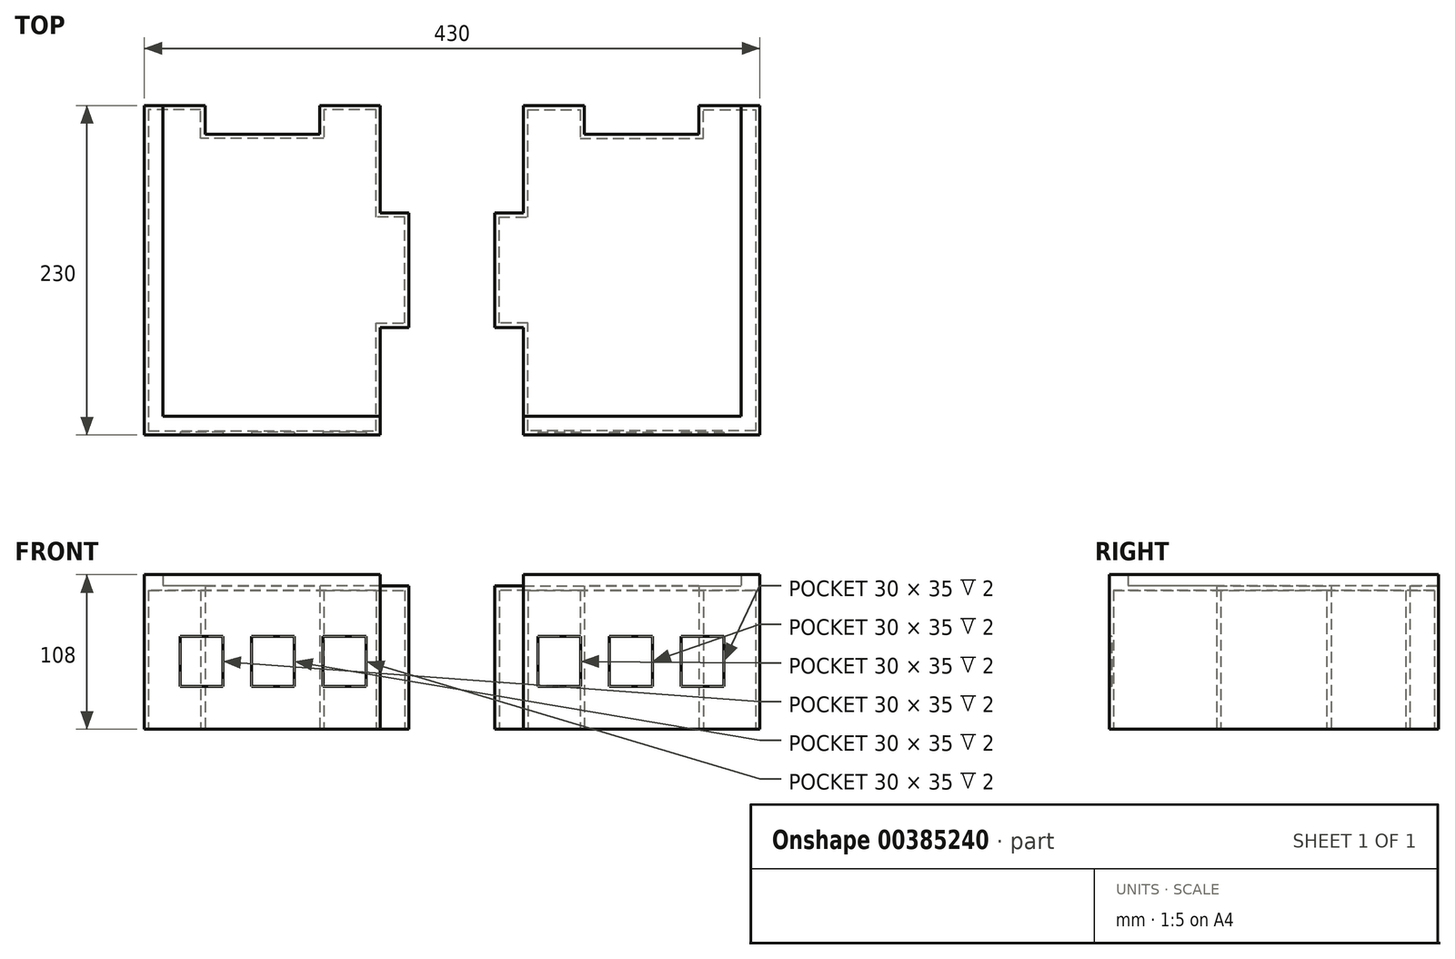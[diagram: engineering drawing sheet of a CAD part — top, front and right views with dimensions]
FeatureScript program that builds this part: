
annotation { "Feature Type Name" : "Feature", "Feature Type Description" : "" }
export const myFeature = defineFeature(function(context is Context, id is Id, definition is map)
    precondition{}
    {
        {
            var Q0;
            Q0=qCreatedBy(makeId("Top.planeOp"),FACE);
            var sketch = newSketch(context, id + "F0", { "sketchPlane" : qUnion([Q0])});
            skLineSegment(sketch, "E0.bottom", {"start": v(0, 0) * mm, "end": v(42.5, 0) * mm});
            skLineSegment(sketch, "E0.top", {"start": v(0, -230) * mm, "end": v(165, -230) * mm});
            skLineSegment(sketch, "E0.left", {"start": v(0, 0) * mm, "end": v(0, -75) * mm});
            skLineSegment(sketch, "E0.right", {"start": v(165, 0) * mm, "end": v(165, -230) * mm});
            skLineSegment(sketch, "E1.bottom", {"start": v(-20, -155) * mm, "end": v(0, -155) * mm});
            skLineSegment(sketch, "E1.top", {"start": v(-20, -75) * mm, "end": v(0, -75) * mm});
            skLineSegment(sketch, "E1.left", {"start": v(-20, -155) * mm, "end": v(-20, -75) * mm});
            skPoint(sketch, "E1.middle", {"position": v(0, -115) * mm});
            skPoint(sketch, "E1.right.start.orphan", {"position": v(20, -155) * mm});
            skPoint(sketch, "E2.orphan", {"position": v(20, -75) * mm});
            skLineSegment(sketch, "E3.trimOffspring", {"start": v(0, -155) * mm, "end": v(0, -230) * mm});
            skLineSegment(sketch, "E4.bottom", {"start": v(122.5, -20) * mm, "end": v(42.5, -20) * mm});
            skLineSegment(sketch, "E4.left", {"start": v(122.5, -20) * mm, "end": v(122.5, 0) * mm});
            skLineSegment(sketch, "E4.right", {"start": v(42.5, -20) * mm, "end": v(42.5, 0) * mm});
            skPoint(sketch, "E4.middle", {"position": v(82.5, 0) * mm});
            skPoint(sketch, "E4.top.end.orphan", {"position": v(42.5, 20) * mm});
            skPoint(sketch, "E5.orphan", {"position": v(122.5, 20) * mm});
            skLineSegment(sketch, "E6.trimOffspring", {"start": v(122.5, 0) * mm, "end": v(165, 0) * mm});
            skLineSegment(sketch, "E7", {"start": v(0, -75) * mm, "end": v(0, 0) * mm});
            skLineSegment(sketch, "E8", {"start": v(42.5, -20) * mm, "end": v(122.5, -20) * mm});
            skLineSegment(sketch, "E9.0", {"start": v(2.5, -152.5) * mm, "end": v(2.5, -227.5) * mm});
            skLineSegment(sketch, "E9.1", {"start": v(125, -22.5) * mm, "end": v(40, -22.5) * mm});
            skLineSegment(sketch, "E9.2", {"start": v(125, -22.5) * mm, "end": v(125, -2.5) * mm});
            skLineSegment(sketch, "E9.3", {"start": v(125, -2.5) * mm, "end": v(162.5, -2.5) * mm});
            skLineSegment(sketch, "E9.4", {"start": v(162.5, -2.5) * mm, "end": v(162.5, -227.5) * mm});
            skLineSegment(sketch, "E9.5", {"start": v(40, -22.5) * mm, "end": v(40, -2.5) * mm});
            skLineSegment(sketch, "E9.6", {"start": v(2.5, -227.5) * mm, "end": v(162.5, -227.5) * mm});
            skLineSegment(sketch, "E9.7", {"start": v(2.5, -2.5) * mm, "end": v(40, -2.5) * mm});
            skLineSegment(sketch, "E9.8", {"start": v(2.5, -77.5) * mm, "end": v(2.5, -2.5) * mm});
            skLineSegment(sketch, "E9.9", {"start": v(-17.5, -77.5) * mm, "end": v(2.5, -77.5) * mm});
            skLineSegment(sketch, "E9.10", {"start": v(-17.5, -152.5) * mm, "end": v(-17.5, -77.5) * mm});
            skLineSegment(sketch, "E9.11", {"start": v(-17.5, -152.5) * mm, "end": v(2.5, -152.5) * mm});
            skSolve(sketch);
        }
        {
            var Q0;
            Q0=makeQuery(id+"F0.imprint","IMPRINT",FACE,{"disambiguationData":[TD([[makeQuery(id+"F0.imprint","IMPRINT",EDGE,{"derivedFrom":sQuery(id+"F0.wireOp",EDGE,"E0.bottom")}),-1.0]])]});
            extrude(context, id + "F1", {"entities" : qUnion([Q0]), "depth" : 100 * mm});
        }
        {
            var Q0;
            Q0=makeQuery(id+"F1.opExtrude","CAP_FACE",FACE,{"disambiguationData":[OSD([sQuery(id+"F0.wireOp",EDGE,"E0.bottom"),sQuery(id+"F0.wireOp",EDGE,"E0.top"),sQuery(id+"F0.wireOp",EDGE,"E0.right"),sQuery(id+"F0.wireOp",EDGE,"E1.bottom"),sQuery(id+"F0.wireOp",EDGE,"E1.top"),sQuery(id+"F0.wireOp",EDGE,"E1.left"),sQuery(id+"F0.wireOp",EDGE,"E3.trimOffspring"),sQuery(id+"F0.wireOp",EDGE,"E4.left"),sQuery(id+"F0.wireOp",EDGE,"E4.right"),sQuery(id+"F0.wireOp",EDGE,"E6.trimOffspring"),sQuery(id+"F0.wireOp",EDGE,"E7"),sQuery(id+"F0.wireOp",EDGE,"E8"),sQuery(id+"F0.wireOp",EDGE,"E9.0"),sQuery(id+"F0.wireOp",EDGE,"E9.1"),sQuery(id+"F0.wireOp",EDGE,"E9.2"),sQuery(id+"F0.wireOp",EDGE,"E9.3"),sQuery(id+"F0.wireOp",EDGE,"E9.4"),sQuery(id+"F0.wireOp",EDGE,"E9.5"),sQuery(id+"F0.wireOp",EDGE,"E9.6"),sQuery(id+"F0.wireOp",EDGE,"E9.7"),sQuery(id+"F0.wireOp",EDGE,"E9.8"),sQuery(id+"F0.wireOp",EDGE,"E9.9"),sQuery(id+"F0.wireOp",EDGE,"E9.10"),sQuery(id+"F0.wireOp",EDGE,"E9.11")])],"isStart":false});
            var sketch = newSketch(context, id + "F2", { "sketchPlane" : qUnion([Q0])});
            skLineSegment(sketch, "E10", {"start": v(0, -230) * mm, "end": v(165, -230) * mm});
            skLineSegment(sketch, "E11", {"start": v(165, -230) * mm, "end": v(165, 0) * mm});
            skLineSegment(sketch, "E12", {"start": v(165, 0) * mm, "end": v(122.5, 0) * mm});
            skLineSegment(sketch, "E13", {"start": v(122.5, 0) * mm, "end": v(122.5, -20) * mm});
            skLineSegment(sketch, "E14", {"start": v(122.5, -20) * mm, "end": v(42.5, -20) * mm});
            skLineSegment(sketch, "E15", {"start": v(42.5, -20) * mm, "end": v(42.5, 0) * mm});
            skLineSegment(sketch, "E16", {"start": v(42.5, 0) * mm, "end": v(0, 0) * mm});
            skLineSegment(sketch, "E17", {"start": v(0, 0) * mm, "end": v(0, -75) * mm});
            skLineSegment(sketch, "E18", {"start": v(0, -75) * mm, "end": v(-20, -75) * mm});
            skLineSegment(sketch, "E19", {"start": v(-20, -75) * mm, "end": v(-20, -155) * mm});
            skLineSegment(sketch, "E20", {"start": v(-20, -155) * mm, "end": v(0, -155) * mm});
            skLineSegment(sketch, "E21", {"start": v(0, -155) * mm, "end": v(0, -230) * mm});
            skSolve(sketch);
        }
        {
            var Q0;
            Q0=qSketchRegion(id+"F2",true);
            extrude(context, id + "F3", {"entities" : qUnion([Q0]), "operationType" : NewBodyOperationType.ADD, "oppositeDirection" : true, "depth" : 3 * mm});
        }
        {
            var Q0;
            Q0=makeQuery(id+"F3.boolean.opBoolean","MERGE",FACE,{"derivedFrom":[makeQuery(id+"F1.opExtrude","CAP_FACE",FACE,{"disambiguationData":[OSD([sQuery(id+"F0.wireOp",EDGE,"E0.bottom"),sQuery(id+"F0.wireOp",EDGE,"E0.top"),sQuery(id+"F0.wireOp",EDGE,"E0.right"),sQuery(id+"F0.wireOp",EDGE,"E1.bottom"),sQuery(id+"F0.wireOp",EDGE,"E1.top"),sQuery(id+"F0.wireOp",EDGE,"E1.left"),sQuery(id+"F0.wireOp",EDGE,"E3.trimOffspring"),sQuery(id+"F0.wireOp",EDGE,"E4.left"),sQuery(id+"F0.wireOp",EDGE,"E4.right"),sQuery(id+"F0.wireOp",EDGE,"E6.trimOffspring"),sQuery(id+"F0.wireOp",EDGE,"E7"),sQuery(id+"F0.wireOp",EDGE,"E8"),sQuery(id+"F0.wireOp",EDGE,"E9.0"),sQuery(id+"F0.wireOp",EDGE,"E9.1"),sQuery(id+"F0.wireOp",EDGE,"E9.2"),sQuery(id+"F0.wireOp",EDGE,"E9.3"),sQuery(id+"F0.wireOp",EDGE,"E9.4"),sQuery(id+"F0.wireOp",EDGE,"E9.5"),sQuery(id+"F0.wireOp",EDGE,"E9.6"),sQuery(id+"F0.wireOp",EDGE,"E9.7"),sQuery(id+"F0.wireOp",EDGE,"E9.8"),sQuery(id+"F0.wireOp",EDGE,"E9.9"),sQuery(id+"F0.wireOp",EDGE,"E9.10"),sQuery(id+"F0.wireOp",EDGE,"E9.11")])],"isStart":false}),makeQuery(id+"F3.opExtrude","CAP_FACE",FACE,{"disambiguationData":[OSD([sQuery(id+"F2.wireOp",EDGE,"E10"),sQuery(id+"F2.wireOp",EDGE,"E11"),sQuery(id+"F2.wireOp",EDGE,"E12"),sQuery(id+"F2.wireOp",EDGE,"E13"),sQuery(id+"F2.wireOp",EDGE,"E14"),sQuery(id+"F2.wireOp",EDGE,"E15"),sQuery(id+"F2.wireOp",EDGE,"E16"),sQuery(id+"F2.wireOp",EDGE,"E17"),sQuery(id+"F2.wireOp",EDGE,"E18"),sQuery(id+"F2.wireOp",EDGE,"E19"),sQuery(id+"F2.wireOp",EDGE,"E20"),sQuery(id+"F2.wireOp",EDGE,"E21")])],"isStart":true})]});
            var sketch = newSketch(context, id + "F4", { "sketchPlane" : qUnion([Q0])});
            skLineSegment(sketch, "E22.bottom", {"start": v(0, -230) * mm, "end": v(165, -230) * mm});
            skLineSegment(sketch, "E22.top", {"start": v(0, -217) * mm, "end": v(152, -217) * mm});
            skLineSegment(sketch, "E22.left", {"start": v(0, -230) * mm, "end": v(0, -217) * mm});
            skLineSegment(sketch, "E22.right", {"start": v(165, -230) * mm, "end": v(165, -217) * mm});
            skLineSegment(sketch, "E23.bottom", {"start": v(165, 0) * mm, "end": v(152, 0) * mm});
            skLineSegment(sketch, "E23.left", {"start": v(165, 0) * mm, "end": v(165, -217) * mm});
            skLineSegment(sketch, "E23.right", {"start": v(152, 0) * mm, "end": v(152, -217) * mm});
            skSolve(sketch);
        }
        {
            var Q0;
            Q0=makeQuery(id+"F4.imprint","IMPRINT",FACE,{"disambiguationData":[TD([[makeQuery(id+"F4.imprint","IMPRINT",EDGE,{"derivedFrom":sQuery(id+"F4.wireOp",EDGE,"E22.bottom")}),1.0]])]});
            extrude(context, id + "F5", {"entities" : qUnion([Q0]), "operationType" : NewBodyOperationType.ADD, "depth" : 8 * mm});
        }
        {
            var Q0;
            Q0=makeQuery(id+"F5.boolean.opBoolean","MERGE",FACE,{"derivedFrom":[makeQuery(id+"F1.opExtrude","SWEPT_FACE",FACE,{"disambiguationData":[OSD([sQuery(id+"F0.wireOp",EDGE,"E0.right")])]}),makeQuery(id+"F5.opExtrude","SWEPT_FACE",FACE,{"disambiguationData":[OSD([sQuery(id+"F4.wireOp",EDGE,"E22.right"),sQuery(id+"F4.wireOp",EDGE,"E23.left")])]})]});
            var sketch = newSketch(context, id + "F6", { "sketchPlane" : qUnion([Q0])});
            skLineSegment(sketch, "E24.bottom", {"start": v(0, 0) * mm, "end": v(-10, 0) * mm, "construction": true});
            skLineSegment(sketch, "E24.top", {"start": v(0, 30) * mm, "end": v(-10, 30) * mm, "construction": true});
            skLineSegment(sketch, "E24.left", {"start": v(0, 0) * mm, "end": v(0, 30) * mm, "construction": true});
            skLineSegment(sketch, "E24.right", {"start": v(-10, 0) * mm, "end": v(-10, 30) * mm, "construction": true});
            skLineSegment(sketch, "E25.bottom", {"start": v(-10, 30) * mm, "end": v(-40, 30) * mm});
            skLineSegment(sketch, "E25.top", {"start": v(-10, 65) * mm, "end": v(-40, 65) * mm});
            skLineSegment(sketch, "E25.left", {"start": v(-10, 30) * mm, "end": v(-10, 65) * mm});
            skLineSegment(sketch, "E25.right", {"start": v(-40, 30) * mm, "end": v(-40, 65) * mm});
            skLineSegment(sketch, "E26.bottom", {"start": v(-40, 30) * mm, "end": v(-60, 30) * mm, "construction": true});
            skLineSegment(sketch, "E26.top", {"start": v(-40, 65) * mm, "end": v(-60, 65) * mm, "construction": true});
            skLineSegment(sketch, "E26.left", {"start": v(-40, 30) * mm, "end": v(-40, 65) * mm, "construction": true});
            skLineSegment(sketch, "E26.right", {"start": v(-60, 30) * mm, "end": v(-60, 65) * mm, "construction": true});
            skLineSegment(sketch, "E27.bottom", {"start": v(-60, 30) * mm, "end": v(-90, 30) * mm});
            skLineSegment(sketch, "E27.top", {"start": v(-60, 65) * mm, "end": v(-90, 65) * mm});
            skLineSegment(sketch, "E27.left", {"start": v(-60, 30) * mm, "end": v(-60, 65) * mm});
            skLineSegment(sketch, "E27.right", {"start": v(-90, 30) * mm, "end": v(-90, 65) * mm});
            skLineSegment(sketch, "E28.bottom", {"start": v(-90, 30) * mm, "end": v(-110, 30) * mm, "construction": true});
            skLineSegment(sketch, "E28.top", {"start": v(-90, 65) * mm, "end": v(-110, 65) * mm, "construction": true});
            skLineSegment(sketch, "E28.left", {"start": v(-90, 30) * mm, "end": v(-90, 65) * mm, "construction": true});
            skLineSegment(sketch, "E28.right", {"start": v(-110, 30) * mm, "end": v(-110, 65) * mm, "construction": true});
            skLineSegment(sketch, "E29.bottom", {"start": v(-110, 30) * mm, "end": v(-140, 30) * mm});
            skLineSegment(sketch, "E29.top", {"start": v(-110, 65) * mm, "end": v(-140, 65) * mm});
            skLineSegment(sketch, "E29.left", {"start": v(-110, 30) * mm, "end": v(-110, 65) * mm});
            skLineSegment(sketch, "E29.right", {"start": v(-140, 30) * mm, "end": v(-140, 65) * mm});
            skLineSegment(sketch, "E30.bottom", {"start": v(-140, 30) * mm, "end": v(-160, 30) * mm, "construction": true});
            skLineSegment(sketch, "E30.top", {"start": v(-140, 65) * mm, "end": v(-160, 65) * mm, "construction": true});
            skLineSegment(sketch, "E30.left", {"start": v(-140, 30) * mm, "end": v(-140, 65) * mm, "construction": true});
            skLineSegment(sketch, "E30.right", {"start": v(-160, 30) * mm, "end": v(-160, 65) * mm, "construction": true});
            skLineSegment(sketch, "E31.bottom", {"start": v(-160, 30) * mm, "end": v(-190, 30) * mm});
            skLineSegment(sketch, "E31.top", {"start": v(-160, 65) * mm, "end": v(-190, 65) * mm});
            skLineSegment(sketch, "E31.left", {"start": v(-160, 30) * mm, "end": v(-160, 65) * mm});
            skLineSegment(sketch, "E31.right", {"start": v(-190, 30) * mm, "end": v(-190, 65) * mm});
            skSolve(sketch);
        }
        {
            var Q0;
            Q0=qSketchRegion(id+"F6",true);
            extrude(context, id + "F7", {"entities" : qUnion([Q0]), "operationType" : NewBodyOperationType.REMOVE, "oppositeDirection" : true, "depth" : 1 * mm});
        }
        {
            var Q0;
            Q0=makeQuery(id+"F1.opExtrude","CAP_FACE",FACE,{"disambiguationData":[OSD([sQuery(id+"F0.wireOp",EDGE,"E0.bottom"),sQuery(id+"F0.wireOp",EDGE,"E0.top"),sQuery(id+"F0.wireOp",EDGE,"E0.right"),sQuery(id+"F0.wireOp",EDGE,"E1.bottom"),sQuery(id+"F0.wireOp",EDGE,"E1.top"),sQuery(id+"F0.wireOp",EDGE,"E1.left"),sQuery(id+"F0.wireOp",EDGE,"E3.trimOffspring"),sQuery(id+"F0.wireOp",EDGE,"E4.left"),sQuery(id+"F0.wireOp",EDGE,"E4.right"),sQuery(id+"F0.wireOp",EDGE,"E6.trimOffspring"),sQuery(id+"F0.wireOp",EDGE,"E7"),sQuery(id+"F0.wireOp",EDGE,"E8"),sQuery(id+"F0.wireOp",EDGE,"E9.0"),sQuery(id+"F0.wireOp",EDGE,"E9.1"),sQuery(id+"F0.wireOp",EDGE,"E9.2"),sQuery(id+"F0.wireOp",EDGE,"E9.3"),sQuery(id+"F0.wireOp",EDGE,"E9.4"),sQuery(id+"F0.wireOp",EDGE,"E9.5"),sQuery(id+"F0.wireOp",EDGE,"E9.6"),sQuery(id+"F0.wireOp",EDGE,"E9.7"),sQuery(id+"F0.wireOp",EDGE,"E9.8"),sQuery(id+"F0.wireOp",EDGE,"E9.9"),sQuery(id+"F0.wireOp",EDGE,"E9.10"),sQuery(id+"F0.wireOp",EDGE,"E9.11")])],"isStart":true});
            var sketch = newSketch(context, id + "F8", { "sketchPlane" : qUnion([Q0])});
            skLineSegment(sketch, "E32", {"start": v(0, 230) * mm, "end": v(0, 155) * mm});
            skLineSegment(sketch, "E33", {"start": v(0, 155) * mm, "end": v(-20, 155) * mm});
            skLineSegment(sketch, "E34", {"start": v(-20, 155) * mm, "end": v(-20, 75) * mm});
            skLineSegment(sketch, "E35", {"start": v(-20, 75) * mm, "end": v(0, 75) * mm});
            skLineSegment(sketch, "E36", {"start": v(0, 75) * mm, "end": v(0, 0) * mm});
            skLineSegment(sketch, "E37", {"start": v(0, 0) * mm, "end": v(42.5, 0) * mm});
            skLineSegment(sketch, "E38", {"start": v(42.5, 0) * mm, "end": v(42.5, 20) * mm});
            skLineSegment(sketch, "E39", {"start": v(42.5, 20) * mm, "end": v(122.5, 20) * mm});
            skLineSegment(sketch, "E40", {"start": v(122.5, 20) * mm, "end": v(122.5, 0) * mm});
            skLineSegment(sketch, "E41", {"start": v(122.5, 0) * mm, "end": v(165, 0) * mm});
            skLineSegment(sketch, "E42", {"start": v(165, 0) * mm, "end": v(165, 230) * mm});
            skLineSegment(sketch, "E43", {"start": v(165, 230) * mm, "end": v(0, 230) * mm});
            skLineSegment(sketch, "E44.0", {"start": v(161.99, 226.99) * mm, "end": v(3.01, 226.99) * mm});
            skLineSegment(sketch, "E44.1", {"start": v(3.01, 78.01) * mm, "end": v(3.01, 3.01) * mm});
            skLineSegment(sketch, "E44.2", {"start": v(-16.99, 78.01) * mm, "end": v(3.01, 78.01) * mm});
            skLineSegment(sketch, "E44.3", {"start": v(-16.99, 151.99) * mm, "end": v(-16.99, 78.01) * mm});
            skLineSegment(sketch, "E44.4", {"start": v(3.01, 151.99) * mm, "end": v(-16.99, 151.99) * mm});
            skLineSegment(sketch, "E44.5", {"start": v(3.01, 3.01) * mm, "end": v(39.49, 3.01) * mm});
            skLineSegment(sketch, "E44.6", {"start": v(3.01, 226.99) * mm, "end": v(3.01, 151.99) * mm});
            skLineSegment(sketch, "E44.7", {"start": v(39.49, 3.01) * mm, "end": v(39.49, 23.01) * mm});
            skLineSegment(sketch, "E44.8", {"start": v(39.49, 23.01) * mm, "end": v(125.51, 23.01) * mm});
            skLineSegment(sketch, "E44.9", {"start": v(125.51, 23.01) * mm, "end": v(125.51, 3.01) * mm});
            skLineSegment(sketch, "E44.10", {"start": v(125.51, 3.01) * mm, "end": v(161.99, 3.01) * mm});
            skLineSegment(sketch, "E44.11", {"start": v(161.99, 3.01) * mm, "end": v(161.99, 226.99) * mm});
            skSolve(sketch);
        }
        {
            var Q0;
            Q0=qCreatedBy(makeId("Right.planeOp"),FACE);
            cPlane(context, id + "F9", {"entities" : qUnion([Q0]), "cplaneType" : CPlaneType.OFFSET, "offset" : 50 * mm, "oppositeDirection" : true, "width" : 150 * mm, "height" : 150 * mm});
        }
        {
            var Q0;
            Q0 = qSketchRegion(id + "F8", true);
            extrude(context, id + "F10", {"entities" : qUnion([Q0]), "operationType" : NewBodyOperationType.ADD, "oppositeDirection" : true, "depth" : 100 * mm});
        }
        {
            var Q0;
            Q0=makeQuery(id+"F5.boolean.opBoolean","MERGE",FACE,{"derivedFrom":[makeQuery(id+"F1.opExtrude","SWEPT_FACE",FACE,{"disambiguationData":[OSD([sQuery(id+"F0.wireOp",EDGE,"E0.top")])]}),makeQuery(id+"F5.opExtrude","SWEPT_FACE",FACE,{"disambiguationData":[OSD([sQuery(id+"F4.wireOp",EDGE,"E22.bottom")])]})]});
            var sketch = newSketch(context, id + "F11", { "sketchPlane" : qUnion([Q0])});
            skLineSegment(sketch, "E45.bottom", {"start": v(0, 0) * mm, "end": v(10, 0) * mm, "construction": true});
            skLineSegment(sketch, "E45.top", {"start": v(0, 30) * mm, "end": v(10, 30) * mm, "construction": true});
            skLineSegment(sketch, "E45.left", {"start": v(0, 0) * mm, "end": v(0, 30) * mm, "construction": true});
            skLineSegment(sketch, "E45.right", {"start": v(10, 0) * mm, "end": v(10, 30) * mm, "construction": true});
            skLineSegment(sketch, "E46.bottom", {"start": v(10, 30) * mm, "end": v(40, 30) * mm});
            skLineSegment(sketch, "E46.top", {"start": v(10, 65) * mm, "end": v(40, 65) * mm});
            skLineSegment(sketch, "E46.left", {"start": v(10, 30) * mm, "end": v(10, 65) * mm});
            skLineSegment(sketch, "E46.right", {"start": v(40, 30) * mm, "end": v(40, 65) * mm});
            skPoint(sketch, "E47.oppositeSnap0", {"position": v(40, 47.5) * mm});
            skLineSegment(sketch, "E47.bottom", {"start": v(40, 30) * mm, "end": v(60, 30) * mm, "construction": true});
            skLineSegment(sketch, "E47.top", {"start": v(40, 47.5) * mm, "end": v(60, 47.5) * mm, "construction": true});
            skLineSegment(sketch, "E47.left", {"start": v(40, 30) * mm, "end": v(40, 47.5) * mm, "construction": true});
            skLineSegment(sketch, "E47.right", {"start": v(60, 30) * mm, "end": v(60, 47.5) * mm, "construction": true});
            skLineSegment(sketch, "E48.bottom", {"start": v(60, 30) * mm, "end": v(90, 30) * mm});
            skLineSegment(sketch, "E48.top", {"start": v(60, 65) * mm, "end": v(90, 65) * mm});
            skLineSegment(sketch, "E48.left", {"start": v(60, 30) * mm, "end": v(60, 65) * mm});
            skLineSegment(sketch, "E48.right", {"start": v(90, 30) * mm, "end": v(90, 65) * mm});
            skLineSegment(sketch, "E49.bottom", {"start": v(90, 30) * mm, "end": v(110, 30) * mm, "construction": true});
            skLineSegment(sketch, "E49.top", {"start": v(90, 51) * mm, "end": v(110, 51) * mm, "construction": true});
            skLineSegment(sketch, "E49.left", {"start": v(90, 30) * mm, "end": v(90, 51) * mm, "construction": true});
            skLineSegment(sketch, "E49.right", {"start": v(110, 30) * mm, "end": v(110, 51) * mm, "construction": true});
            skLineSegment(sketch, "E50.bottom", {"start": v(110, 30) * mm, "end": v(140, 30) * mm});
            skLineSegment(sketch, "E50.top", {"start": v(110, 65) * mm, "end": v(140, 65) * mm});
            skLineSegment(sketch, "E50.left", {"start": v(110, 30) * mm, "end": v(110, 65) * mm});
            skLineSegment(sketch, "E50.right", {"start": v(140, 30) * mm, "end": v(140, 65) * mm});
            skSolve(sketch);
        }
        {
            var Q0;
            Q0=qSketchRegion(id+"F11",true);
            extrude(context, id + "F12", {"entities" : qUnion([Q0]), "operationType" : NewBodyOperationType.REMOVE, "oppositeDirection" : true, "depth" : 2 * mm});
        }
        {
            var Q0;
            Q0=makeQuery(id+"F1.opExtrude","SWEPT_BODY",BODY,{"disambiguationData":[OSD([sQuery(id+"F0.wireOp",EDGE,"E0.bottom"),sQuery(id+"F0.wireOp",EDGE,"E0.top"),sQuery(id+"F0.wireOp",EDGE,"E0.right"),sQuery(id+"F0.wireOp",EDGE,"E1.bottom"),sQuery(id+"F0.wireOp",EDGE,"E1.top"),sQuery(id+"F0.wireOp",EDGE,"E1.left"),sQuery(id+"F0.wireOp",EDGE,"E3.trimOffspring"),sQuery(id+"F0.wireOp",EDGE,"E4.left"),sQuery(id+"F0.wireOp",EDGE,"E4.right"),sQuery(id+"F0.wireOp",EDGE,"E6.trimOffspring"),sQuery(id+"F0.wireOp",EDGE,"E7"),sQuery(id+"F0.wireOp",EDGE,"E8"),sQuery(id+"F0.wireOp",EDGE,"E9.0"),sQuery(id+"F0.wireOp",EDGE,"E9.1"),sQuery(id+"F0.wireOp",EDGE,"E9.2"),sQuery(id+"F0.wireOp",EDGE,"E9.3"),sQuery(id+"F0.wireOp",EDGE,"E9.4"),sQuery(id+"F0.wireOp",EDGE,"E9.5"),sQuery(id+"F0.wireOp",EDGE,"E9.6"),sQuery(id+"F0.wireOp",EDGE,"E9.7"),sQuery(id+"F0.wireOp",EDGE,"E9.8"),sQuery(id+"F0.wireOp",EDGE,"E9.9"),sQuery(id+"F0.wireOp",EDGE,"E9.10"),sQuery(id+"F0.wireOp",EDGE,"E9.11")])]});
            var Q1;
            Q1=qCreatedBy(id+"F9.planeOp",FACE);
            mirror(context, id + "F13", {"entities" : qUnion([Q0]), "mirrorPlane" : qUnion([Q1])});
        }
    });
